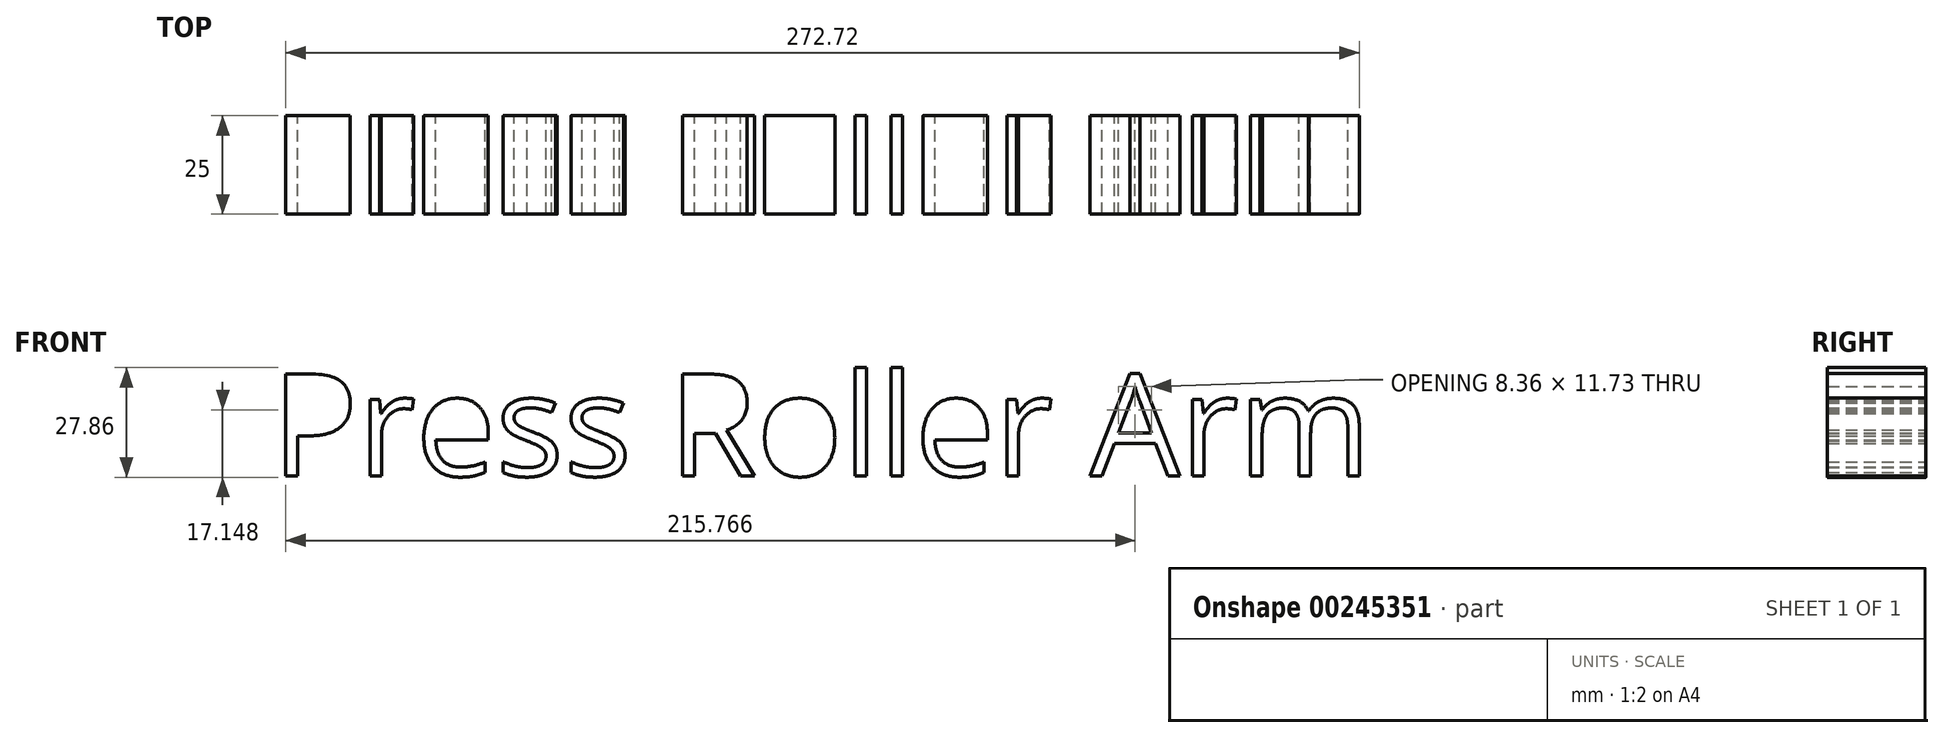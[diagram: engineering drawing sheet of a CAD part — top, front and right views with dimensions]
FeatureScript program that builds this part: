
annotation { "Feature Type Name" : "Feature", "Feature Type Description" : "" }
export const myFeature = defineFeature(function(context is Context, id is Id, definition is map)
    precondition{}
    {
        {
            var Q0;
            Q0=qCreatedBy(makeId("Front.planeOp"),FACE);
            var sketch = newSketch(context, id + "F0", { "sketchPlane" : qUnion([Q0])});
            skLineSegment(sketch, "E0", {"start": v(0, 0) * mm, "end": v(150, 0) * mm});
            skLineSegment(sketch, "E1", {"start": v(150, 0) * mm, "end": v(225.06, -130) * mm});
            skLineSegment(sketch, "E2", {"start": v(225.06, -130) * mm, "end": v(375.06, -130) * mm});
            skLineSegment(sketch, "E3", {"start": v(0, 0) * mm, "end": v(-90, 0) * mm});
            skText(sketch, "E4", { "text": "Press Roller Arm", "fontName": "OpenSans-Regular.ttf"});
            skCircle(sketch, "E5", {"center": v(483.12, -21.6) * mm, "radius": 36 * mm});
            skCircle(sketch, "E6", {"center": v(563.12, -21.6) * mm, "radius": 36 * mm});
            skLineSegment(sketch, "E7", {"start": v(483.12, -21.6) * mm, "end": v(563.12, -21.6) * mm});
            skLineSegment(sketch, "E8", {"start": v(523.12, -21.6) * mm, "end": v(523.12, 73.36) * mm});
            skCircle(sketch, "E9", {"center": v(523.12, 23.13) * mm, "radius": 24 * mm});
            skCircle(sketch, "E10", {"center": v(668.9, -21.6) * mm, "radius": 36 * mm});
            skCircle(sketch, "E11", {"center": v(764.9, -21.6) * mm, "radius": 36 * mm});
            skLineSegment(sketch, "E12", {"start": v(668.9, -21.6) * mm, "end": v(764.9, -21.6) * mm});
            skLineSegment(sketch, "E13", {"start": v(716.9, -21.6) * mm, "end": v(716.9, 81.87) * mm});
            skCircle(sketch, "E14", {"center": v(716.9, 23.13) * mm, "radius": 29.6 * mm});
            const initialGuessF0  = {"E4": [0.0337, -0.13694, 1, 0, 0.02606]};
            skSetInitialGuess(sketch, initialGuessF0);
            skSolve(sketch);
        }
        {
            var Q0;
            {var subQ5=sQuery(id+"F0.wireOp",EDGE,"E4.sketch_text.stroke-204");Q0=makeQuery(id+"F0.imprint","IMPRINT",FACE,{"disambiguationData":[TD([[makeQuery(id+"F0.imprint","IMPRINT",EDGE,{"derivedFrom":subQ5}),-1.0]])]});}
            var Q1;
            {var subQ5=sQuery(id+"F0.wireOp",EDGE,"E4.sketch_text.stroke-211");Q1=makeQuery(id+"F0.imprint","IMPRINT",FACE,{"disambiguationData":[TD([[makeQuery(id+"F0.imprint","IMPRINT",EDGE,{"derivedFrom":subQ5}),-1.0]])]});}
            var Q2;
            {var subQ10=sQuery(id+"F0.wireOp",EDGE,"E4.sketch_text.stroke-199");Q2=makeQuery(id+"F0.imprint","IMPRINT",FACE,{"disambiguationData":[TD([[makeQuery(id+"F0.imprint","IMPRINT",EDGE,{"derivedFrom":subQ10}),-1.0]])]});}
            var Q3;
            {var subQ5=sQuery(id+"F0.wireOp",EDGE,"E4.sketch_text.stroke-225");Q3=makeQuery(id+"F0.imprint","IMPRINT",FACE,{"disambiguationData":[TD([[makeQuery(id+"F0.imprint","IMPRINT",EDGE,{"derivedFrom":subQ5}),-1.0]])]});}
            var Q4;
            Q4=makeQuery(id+"F0.imprint","IMPRINT",FACE,{"disambiguationData":[TD([[makeQuery(id+"F0.imprint","IMPRINT",EDGE,{"derivedFrom":sQuery(id+"F0.wireOp",EDGE,"E4.sketch_text.stroke-185")}),-1.0]])]});
            var Q5;
            {var subQ5=sQuery(id+"F0.wireOp",EDGE,"E4.sketch_text.stroke-191");Q5=makeQuery(id+"F0.imprint","IMPRINT",FACE,{"disambiguationData":[TD([[makeQuery(id+"F0.imprint","IMPRINT",EDGE,{"derivedFrom":subQ5}),-1.0]])]});}
            var Q6;
            {var subQ7=sQuery(id+"F0.wireOp",EDGE,"E4.sketch_text.stroke-173");Q6=makeQuery(id+"F0.imprint","IMPRINT",FACE,{"disambiguationData":[TD([[makeQuery(id+"F0.imprint","IMPRINT",EDGE,{"derivedFrom":subQ7}),-1.0]])]});}
            var Q7;
            {var subQ5=sQuery(id+"F0.wireOp",EDGE,"E4.sketch_text.stroke-175");Q7=makeQuery(id+"F0.imprint","IMPRINT",FACE,{"disambiguationData":[TD([[makeQuery(id+"F0.imprint","IMPRINT",EDGE,{"derivedFrom":subQ5}),-1.0]])]});}
            var Q8;
            {var subQ5=sQuery(id+"F0.wireOp",EDGE,"E4.sketch_text.stroke-179");Q8=makeQuery(id+"F0.imprint","IMPRINT",FACE,{"disambiguationData":[TD([[makeQuery(id+"F0.imprint","IMPRINT",EDGE,{"derivedFrom":subQ5}),-1.0]])]});}
            var Q9;
            Q9=makeQuery(id+"F0.imprint","IMPRINT",FACE,{"disambiguationData":[TD([[makeQuery(id+"F0.imprint","IMPRINT",EDGE,{"derivedFrom":sQuery(id+"F0.wireOp",EDGE,"E4.sketch_text.stroke-47")}),-1.0]])]});
            var Q10;
            Q10=makeQuery(id+"F0.imprint","IMPRINT",FACE,{"disambiguationData":[TD([[makeQuery(id+"F0.imprint","IMPRINT",EDGE,{"derivedFrom":sQuery(id+"F0.wireOp",EDGE,"E4.sketch_text.stroke-159")}),-1.0]])]});
            var Q11;
            Q11=makeQuery(id+"F0.imprint","IMPRINT",FACE,{"disambiguationData":[TD([[makeQuery(id+"F0.imprint","IMPRINT",EDGE,{"derivedFrom":sQuery(id+"F0.wireOp",EDGE,"E4.sketch_text.stroke-0")}),-1.0]])]});
            var Q12;
            Q12=makeQuery(id+"F0.imprint","IMPRINT",FACE,{"disambiguationData":[TD([[makeQuery(id+"F0.imprint","IMPRINT",EDGE,{"derivedFrom":sQuery(id+"F0.wireOp",EDGE,"E4.sketch_text.stroke-8")}),1.0]])]});
            var Q13;
            Q13=makeQuery(id+"F0.imprint","IMPRINT",FACE,{"disambiguationData":[TD([[makeQuery(id+"F0.imprint","IMPRINT",EDGE,{"derivedFrom":sQuery(id+"F0.wireOp",EDGE,"E4.sketch_text.stroke-28")}),-1.0]])]});
            var Q14;
            Q14=makeQuery(id+"F0.imprint","IMPRINT",FACE,{"disambiguationData":[TD([[makeQuery(id+"F0.imprint","IMPRINT",EDGE,{"derivedFrom":sQuery(id+"F0.wireOp",EDGE,"E4.sketch_text.stroke-42")}),1.0]])]});
            var Q15;
            Q15=makeQuery(id+"F0.imprint","IMPRINT",FACE,{"disambiguationData":[TD([[makeQuery(id+"F0.imprint","IMPRINT",EDGE,{"derivedFrom":sQuery(id+"F0.wireOp",EDGE,"E4.sketch_text.stroke-97")}),-1.0]])]});
            var Q16;
            Q16=makeQuery(id+"F0.imprint","IMPRINT",FACE,{"disambiguationData":[TD([[makeQuery(id+"F0.imprint","IMPRINT",EDGE,{"derivedFrom":sQuery(id+"F0.wireOp",EDGE,"E4.sketch_text.stroke-108")}),1.0]])]});
            var Q17;
            Q17=makeQuery(id+"F0.imprint","IMPRINT",FACE,{"disambiguationData":[TD([[makeQuery(id+"F0.imprint","IMPRINT",EDGE,{"derivedFrom":sQuery(id+"F0.wireOp",EDGE,"E4.sketch_text.stroke-115")}),-1.0]])]});
            var Q18;
            Q18=makeQuery(id+"F0.imprint","IMPRINT",FACE,{"disambiguationData":[TD([[makeQuery(id+"F0.imprint","IMPRINT",EDGE,{"derivedFrom":sQuery(id+"F0.wireOp",EDGE,"E4.sketch_text.stroke-124")}),1.0]])]});
            var Q19;
            Q19=makeQuery(id+"F0.imprint","IMPRINT",FACE,{"disambiguationData":[TD([[makeQuery(id+"F0.imprint","IMPRINT",EDGE,{"derivedFrom":sQuery(id+"F0.wireOp",EDGE,"E4.sketch_text.stroke-140")}),-1.0]])]});
            var Q20;
            Q20=makeQuery(id+"F0.imprint","IMPRINT",FACE,{"disambiguationData":[TD([[makeQuery(id+"F0.imprint","IMPRINT",EDGE,{"derivedFrom":sQuery(id+"F0.wireOp",EDGE,"E4.sketch_text.stroke-154")}),1.0]])]});
            var Q21;
            Q21=makeQuery(id+"F0.imprint","IMPRINT",FACE,{"disambiguationData":[TD([[makeQuery(id+"F0.imprint","IMPRINT",EDGE,{"derivedFrom":sQuery(id+"F0.wireOp",EDGE,"E4.sketch_text.stroke-15")}),-1.0]])]});
            var Q22;
            Q22=makeQuery(id+"F0.imprint","IMPRINT",FACE,{"disambiguationData":[TD([[makeQuery(id+"F0.imprint","IMPRINT",EDGE,{"derivedFrom":sQuery(id+"F0.wireOp",EDGE,"E4.sketch_text.stroke-72")}),-1.0]])]});
            var Q23;
            Q23=makeQuery(id+"F0.imprint","IMPRINT",FACE,{"disambiguationData":[TD([[makeQuery(id+"F0.imprint","IMPRINT",EDGE,{"derivedFrom":sQuery(id+"F0.wireOp",EDGE,"E4.sketch_text.stroke-132")}),-1.0]])]});
            var Q24;
            Q24=makeQuery(id+"F0.imprint","IMPRINT",FACE,{"disambiguationData":[TD([[makeQuery(id+"F0.imprint","IMPRINT",EDGE,{"derivedFrom":sQuery(id+"F0.wireOp",EDGE,"E4.sketch_text.stroke-136")}),-1.0]])]});
            var Q25;
            {var subQ5=sQuery(id+"F0.wireOp",EDGE,"E4.sketch_text.stroke-165");Q25=makeQuery(id+"F0.imprint","IMPRINT",FACE,{"disambiguationData":[TD([[makeQuery(id+"F0.imprint","IMPRINT",EDGE,{"derivedFrom":subQ5}),-1.0]])]});}
            extrude(context, id + "F1", {"entities" : qUnion([Q0, Q1, Q2, Q3, Q4, Q5, Q6, Q7, Q8, Q9, Q10, Q11, Q12, Q13, Q14, Q15, Q16, Q17, Q18, Q19, Q20, Q21, Q22, Q23, Q24, Q25]), "offsetDistance" : 25 * mm, "depth" : 25 * mm});
        }
    });
